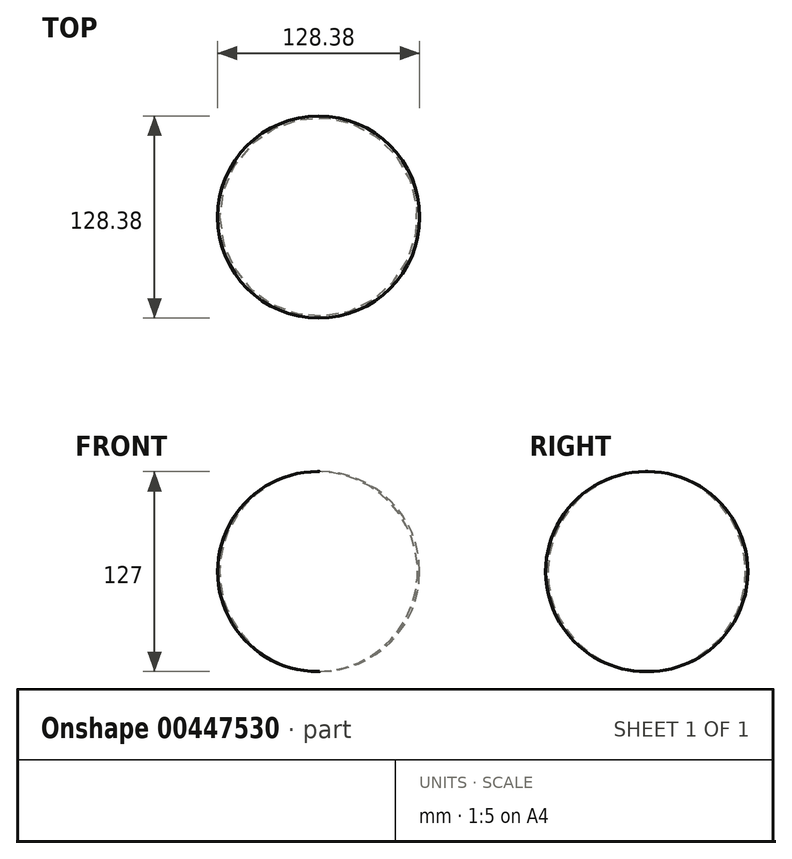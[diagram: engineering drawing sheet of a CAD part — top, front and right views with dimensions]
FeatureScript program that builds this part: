
annotation { "Feature Type Name" : "Feature", "Feature Type Description" : "" }
export const myFeature = defineFeature(function(context is Context, id is Id, definition is map)
    precondition{}
    {
        {
            var Q0;
            Q0=qCreatedBy(makeId("Front.planeOp"),FACE);
            var sketch = newSketch(context, id + "F0", { "sketchPlane" : qUnion([Q0])});
            skLineSegment(sketch, "E0", {"start": v(0, 74.08) * mm, "end": v(0, -52.92) * mm});
            skArc(sketch, "E1", {"start": v(0, -52.92) * mm, "mid": v(62.81, 10.58) * mm, "end": v(0, 74.08) * mm});
            skSolve(sketch);
        }
        {
            var Q0;
            {var subQ0=sQuery(id+"F0.wireOp",EDGE,"E1");Q0=makeQuery(id+"F0.imprint","IMPRINT",FACE,{"disambiguationData":[TD([[makeQuery(id+"F0.imprint","IMPRINT",EDGE,{"derivedFrom":subQ0}),1.0]])]});}
            var Q1;
            Q1=sQuery(id+"F0.wireOp",EDGE,"E0");
            revolve(context, id + "F1", {"entities" : qUnion([Q0]), "axis" : qUnion([Q1]), "revolveType" : RevolveType.FULL});
        }
    });
